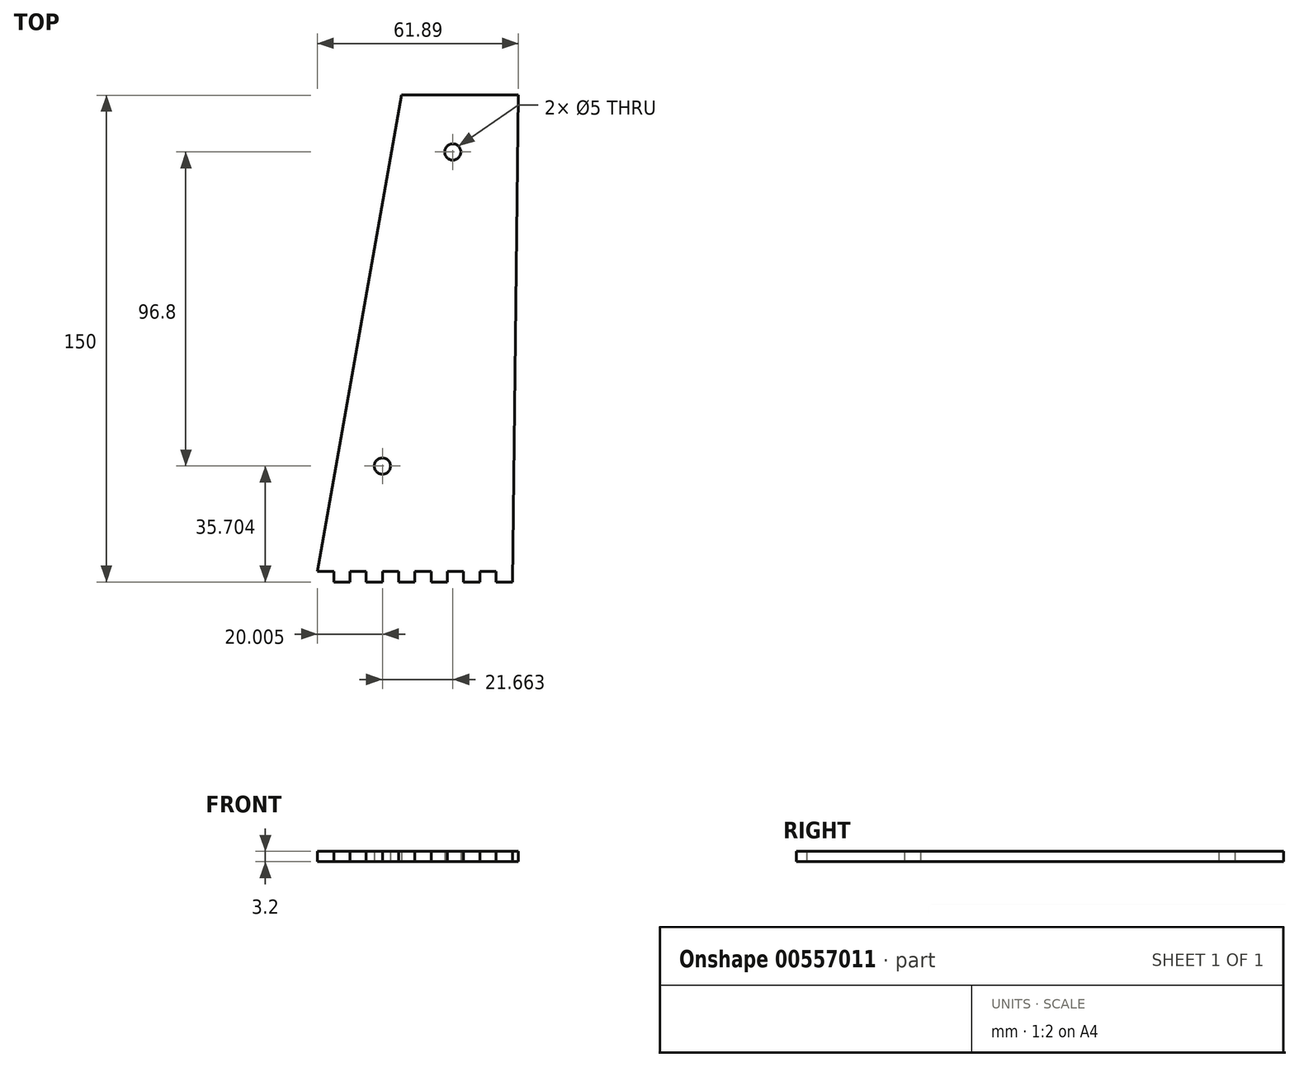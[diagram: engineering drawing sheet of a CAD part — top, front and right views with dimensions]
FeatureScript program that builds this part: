
annotation { "Feature Type Name" : "Feature", "Feature Type Description" : "" }
export const myFeature = defineFeature(function(context is Context, id is Id, definition is map)
    precondition{}
    {
        {
            var Q0;
            Q0=qCreatedBy(makeId("Top.planeOp"),FACE);
            var sketch = newSketch(context, id + "F0", { "sketchPlane" : qUnion([Q0])});
            skLineSegment(sketch, "E0.bottom", {"start": v(-1.94, 100.21) * mm, "end": v(34.06, 100.21) * mm});
            skLineSegment(sketch, "E0.top", {"start": v(-22.83, -49.79) * mm, "end": v(-17.83, -49.79) * mm});
            skLineSegment(sketch, "E0.right", {"start": v(34.06, 100.21) * mm, "end": v(32.17, -49.79) * mm});
            skLineSegment(sketch, "E1.bottom", {"start": v(-27.83, -46.59) * mm, "end": v(-22.83, -46.59) * mm});
            skLineSegment(sketch, "E1.right", {"start": v(-22.83, -46.59) * mm, "end": v(-22.83, -49.79) * mm});
            skLineSegment(sketch, "E2.bottom", {"start": v(-17.83, -46.59) * mm, "end": v(-12.83, -46.59) * mm});
            skLineSegment(sketch, "E2.left", {"start": v(-17.83, -46.59) * mm, "end": v(-17.83, -49.79) * mm});
            skLineSegment(sketch, "E2.right", {"start": v(-12.83, -46.59) * mm, "end": v(-12.83, -49.79) * mm});
            skLineSegment(sketch, "E3.bottom", {"start": v(-7.83, -46.59) * mm, "end": v(-2.83, -46.59) * mm});
            skLineSegment(sketch, "E3.left", {"start": v(-7.83, -46.59) * mm, "end": v(-7.83, -49.79) * mm});
            skLineSegment(sketch, "E3.right", {"start": v(-2.83, -46.59) * mm, "end": v(-2.83, -49.79) * mm});
            skLineSegment(sketch, "E4.bottom", {"start": v(2.17, -46.59) * mm, "end": v(7.17, -46.59) * mm});
            skLineSegment(sketch, "E4.left", {"start": v(2.17, -46.59) * mm, "end": v(2.17, -49.79) * mm});
            skLineSegment(sketch, "E4.right", {"start": v(7.17, -46.59) * mm, "end": v(7.17, -49.79) * mm});
            skLineSegment(sketch, "E5.bottom", {"start": v(12.17, -46.59) * mm, "end": v(17.17, -46.59) * mm});
            skLineSegment(sketch, "E5.left", {"start": v(12.17, -46.59) * mm, "end": v(12.17, -49.79) * mm});
            skLineSegment(sketch, "E5.right", {"start": v(17.17, -46.59) * mm, "end": v(17.17, -49.79) * mm});
            skLineSegment(sketch, "E6.bottom", {"start": v(22.17, -46.59) * mm, "end": v(27.17, -46.59) * mm});
            skLineSegment(sketch, "E6.left", {"start": v(22.17, -46.59) * mm, "end": v(22.17, -49.79) * mm});
            skLineSegment(sketch, "E6.right", {"start": v(27.17, -46.59) * mm, "end": v(27.17, -49.79) * mm});
            skLineSegment(sketch, "E7.trimOffspring", {"start": v(-12.83, -49.79) * mm, "end": v(-7.83, -49.79) * mm});
            skLineSegment(sketch, "E8.trimOffspring", {"start": v(-2.83, -49.79) * mm, "end": v(2.17, -49.79) * mm});
            skLineSegment(sketch, "E9.trimOffspring", {"start": v(7.17, -49.79) * mm, "end": v(12.17, -49.79) * mm});
            skLineSegment(sketch, "E10.trimOffspring", {"start": v(17.17, -49.79) * mm, "end": v(22.17, -49.79) * mm});
            skLineSegment(sketch, "E11.trimOffspring", {"start": v(27.17, -49.79) * mm, "end": v(32.17, -49.79) * mm});
            skLineSegment(sketch, "E12", {"start": v(-27.83, -46.59) * mm, "end": v(-1.94, 100.21) * mm});
            skCircle(sketch, "E13", {"center": v(13.84, 82.71) * mm, "radius": 2.5 * mm});
            skCircle(sketch, "E14", {"center": v(-7.83, -14.09) * mm, "radius": 2.5 * mm});
            skSolve(sketch);
        }
        {
            var Q0;
            Q0=qSketchRegion(id+"F0",true);
            extrude(context, id + "F1", {"entities" : qUnion([Q0]), "depth" : 3.2 * mm});
        }
    });
